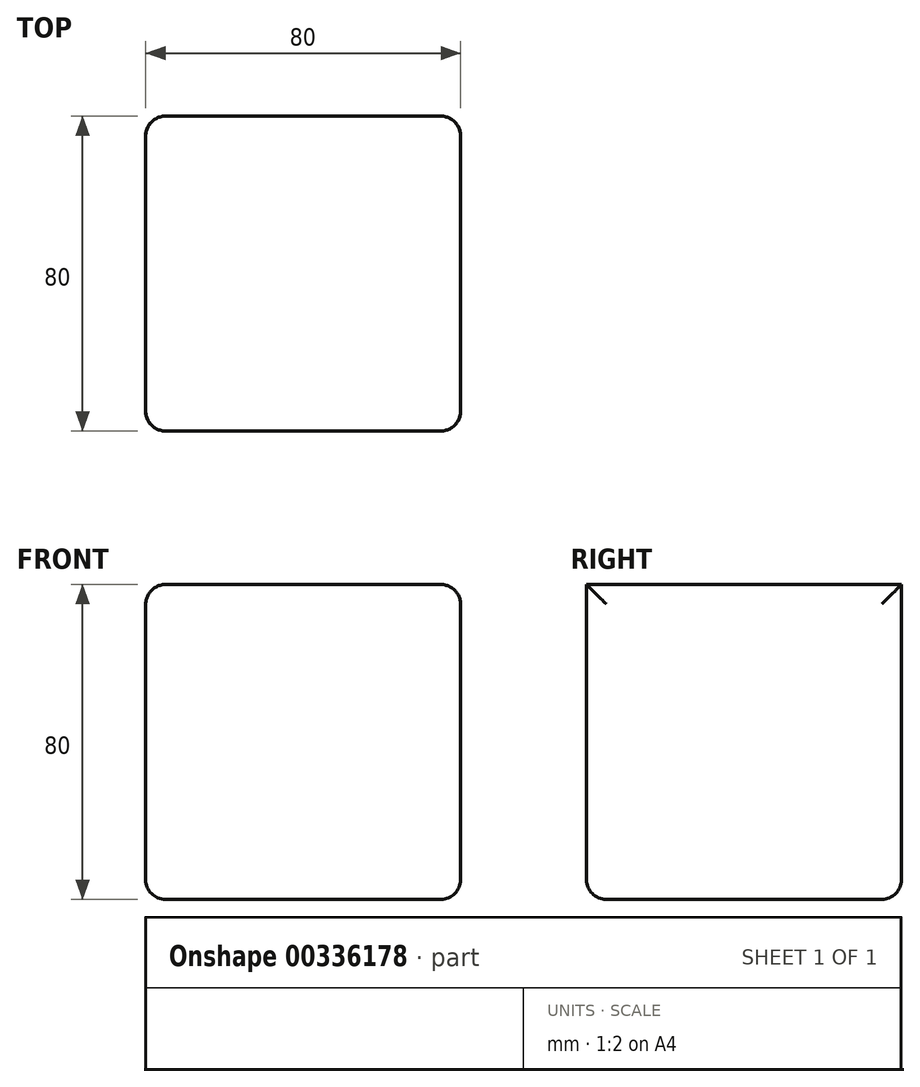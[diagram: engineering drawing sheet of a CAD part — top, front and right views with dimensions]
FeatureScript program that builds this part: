
annotation { "Feature Type Name" : "Feature", "Feature Type Description" : "" }
export const myFeature = defineFeature(function(context is Context, id is Id, definition is map)
    precondition{}
    {
        {
            var Q0;
            Q0=qCreatedBy(makeId("Top.planeOp"),FACE);
            var sketch = newSketch(context, id + "F0", { "sketchPlane" : qUnion([Q0])});
            skLineSegment(sketch, "E0.bottom", {"start": v(-40, 40) * mm, "end": v(40, 40) * mm});
            skLineSegment(sketch, "E0.top", {"start": v(-40, -40) * mm, "end": v(40, -40) * mm});
            skLineSegment(sketch, "E0.left", {"start": v(-40, 40) * mm, "end": v(-40, -40) * mm});
            skLineSegment(sketch, "E0.right", {"start": v(40, 40) * mm, "end": v(40, -40) * mm});
            skPoint(sketch, "E0.middle", {"position": v(0, 0) * mm});
            skSolve(sketch);
        }
        {
            var Q0;
            Q0=makeQuery(id+"F0.imprint","IMPRINT",FACE,{"disambiguationData":[TD([[makeQuery(id+"F0.imprint","IMPRINT",EDGE,{"derivedFrom":sQuery(id+"F0.wireOp",EDGE,"E0.bottom")}),-1.0]])]});
            extrude(context, id + "F1", {"entities" : qUnion([Q0]), "depth" : 80 * mm});
        }
        {
            var Q0;
            Q0=makeQuery(id+"F1.opExtrude","SWEPT_FACE",FACE,{"disambiguationData":[OSD([sQuery(id+"F0.wireOp",EDGE,"E0.left")])]});
            var Q1;
            Q1=makeQuery(id+"F1.opExtrude","CAP_FACE",FACE,{"disambiguationData":[OSD([sQuery(id+"F0.wireOp",EDGE,"E0.bottom"),sQuery(id+"F0.wireOp",EDGE,"E0.top"),sQuery(id+"F0.wireOp",EDGE,"E0.left"),sQuery(id+"F0.wireOp",EDGE,"E0.right")])],"isStart":true});
            var Q2;
            Q2=makeQuery(id+"F1.opExtrude","SWEPT_FACE",FACE,{"disambiguationData":[OSD([sQuery(id+"F0.wireOp",EDGE,"E0.right")])]});
            fillet(context, id + "F2", {"entities" : qUnion([Q0, Q1, Q2]), "radius" : 5 * mm, "tangentPropagation" : true, "allowEdgeOverflow" : false});
        }
    });
